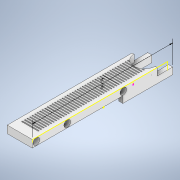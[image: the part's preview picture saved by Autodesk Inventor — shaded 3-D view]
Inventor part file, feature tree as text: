
AUTODESK INVENTOR PART (.ipt)
format: ipt  version: 2022.1 (Build 261234000, 234)  size: 499,200 bytes
history: native  units: in
note: dims shown in document units (in); Inventor stores cm internally (conversion verified against a paired STEP export)
features: sketch x12, other x5, extrude x5
ambient origin geometry x8: Origin, YZ Plane, XZ Plane, XY Plane, X Axis, Y Axis, Z Axis, Center Point
bodies: Solid1 (feature_tree)
feature tree (22):
  other  "purple reign bridge.ipt"
  other  "Annotations"
  extrude  "Extrusion1"  Depth=0.5in TaperAngle=0.0deg
  extrude  "Extrusion2"  Depth=0.2756in TaperAngle=0.0deg
  extrude  "Extrusion3"  Depth=0.3937in TaperAngle=0.0deg
  extrude  "Extrusion4"  TaperAngle=0.0deg  [1 undecoded]
  extrude  "Extrusion5"  Depth=0.315in TaperAngle=0.0deg
  other  "Solid1::purple reign bridge.ipt"
  other  "TaggingFeature1"
  sketch  "Sketch1"  dims[d0=0.3937in d1=0.5in d2=0.0in]
  sketch  "Sketch2"  dims[d3=0.063in d4=0.0394in d5=0.1772in d6=0.1772in d7=0.0394in d8=0.2756in d9=0.0in]
  sketch  "Sketch3"  dims[d10=0.0787in d11=0.3937in d12=0.0in]
  sketch  "Sketch5"  dims[d13=1.0in d14=0.0in d15=0.0in]
  sketch  "Sketch7"  dims[d19=0.1526in d20=0.3096in d21=6.6598in]
  sketch  "Sketch6"  dims[d16=2.3622in d17=0.315in d18=0.0in]
  sketch  "Sketch12"
  sketch  "Sketch10"
  sketch  "Sketch11"
  sketch  "Sketch13"
  sketch  "Sketch14"
  sketch  "Sketch15"
  other  "Linear Dimension 1"
note: 1 required parameter value undecoded (feature->parameter linkage not recoverable at this tier; creation-order binding heuristic only, values carry confidence <= 0.55)
